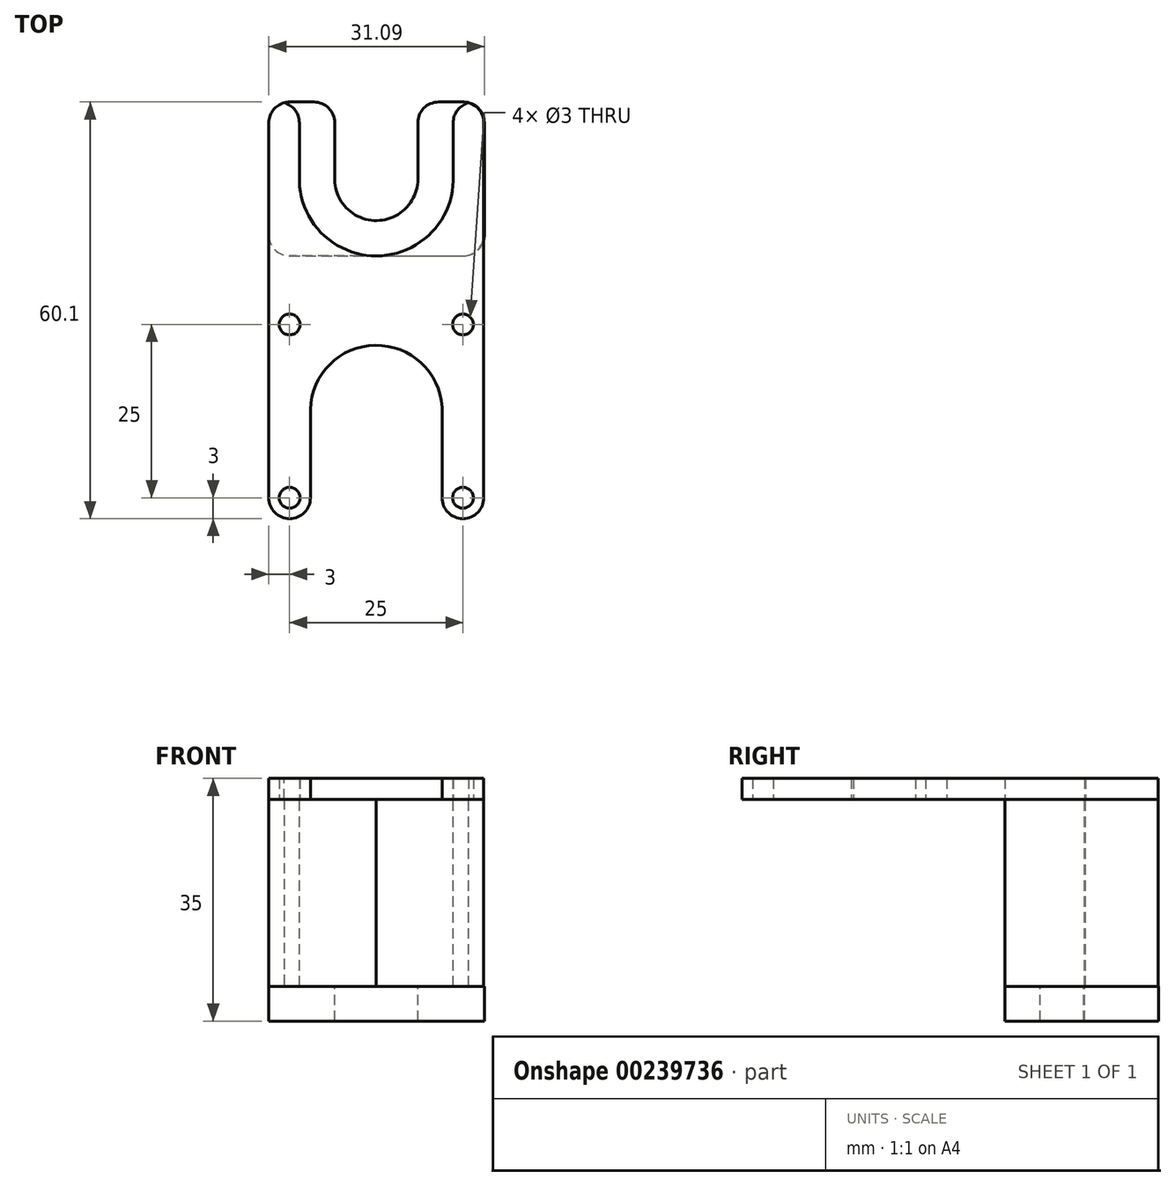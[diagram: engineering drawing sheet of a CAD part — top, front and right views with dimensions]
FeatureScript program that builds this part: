
annotation { "Feature Type Name" : "Feature", "Feature Type Description" : "" }
export const myFeature = defineFeature(function(context is Context, id is Id, definition is map)
    precondition{}
    {
        {
            var Q0;
            Q0=qCreatedBy(makeId("Top.planeOp"),FACE);
            var sketch = newSketch(context, id + "F0", { "sketchPlane" : qUnion([Q0])});
            skCircle(sketch, "E0", {"center": v(-12.5, 0) * mm, "radius": 1.5 * mm});
            skCircle(sketch, "E1", {"center": v(12.5, 0) * mm, "radius": 1.5 * mm});
            skCircle(sketch, "E2", {"center": v(-12.5, 25) * mm, "radius": 1.5 * mm});
            skCircle(sketch, "E3", {"center": v(12.5, 25) * mm, "radius": 1.5 * mm});
            skLineSegment(sketch, "E4.bottom", {"start": v(-15.5, 57.1) * mm, "end": v(-11.1, 57.1) * mm});
            skLineSegment(sketch, "E4.top", {"start": v(-12.5, -3) * mm, "end": v(-12.5, -3) * mm});
            skLineSegment(sketch, "E4.left", {"start": v(-15.5, 57.1) * mm, "end": v(-15.5, 0) * mm});
            skLineSegment(sketch, "E4.right", {"start": v(15.5, 57.1) * mm, "end": v(15.5, 0) * mm});
            skArc(sketch, "E5", {"start": v(9.48, 11.96) * mm, "mid": v(0.16, 22) * mm, "end": v(-9.5, 12.28) * mm});
            skLineSegment(sketch, "E6", {"start": v(-9.5, 12.72) * mm, "end": v(-9.5, 0) * mm});
            skLineSegment(sketch, "E7", {"start": v(9.48, 13.04) * mm, "end": v(9.48, 0) * mm});
            skLineSegment(sketch, "E8.trimOffspring", {"start": v(12.48, -3) * mm, "end": v(12.5, -3) * mm});
            skArc(sketch, "E9", {"start": v(-11.1, 46.4) * mm, "mid": v(0.05, 34.9) * mm, "end": v(11.09, 46.5) * mm});
            skPoint(sketch, "E10.visualSharp", {"position": v(15.5, -3) * mm});
            skArc(sketch, "E10.filletArc", {"start": v(12.5, -3) * mm, "mid": v(14.62, -2.12) * mm, "end": v(15.5, 0) * mm});
            skPoint(sketch, "E11.visualSharp", {"position": v(-15.5, -3) * mm});
            skArc(sketch, "E11.filletArc", {"start": v(-15.5, 0) * mm, "mid": v(-14.62, -2.12) * mm, "end": v(-12.5, -3) * mm});
            skPoint(sketch, "E12.visualSharp", {"position": v(-9.5, -3) * mm});
            skArc(sketch, "E12.filletArc", {"start": v(-12.5, -3) * mm, "mid": v(-10.38, -2.12) * mm, "end": v(-9.5, 0) * mm});
            skPoint(sketch, "E13.visualSharp", {"position": v(9.48, -3) * mm});
            skArc(sketch, "E13.filletArc", {"start": v(9.48, 0) * mm, "mid": v(10.36, -2.12) * mm, "end": v(12.48, -3) * mm});
            skLineSegment(sketch, "E14", {"start": v(-11.1, 46.4) * mm, "end": v(-11.1, 57.1) * mm});
            skLineSegment(sketch, "E15", {"start": v(11.09, 46.5) * mm, "end": v(11.09, 57.1) * mm});
            skLineSegment(sketch, "E16.trimOffspring", {"start": v(11.09, 57.1) * mm, "end": v(15.5, 57.1) * mm});
            skSolve(sketch);
        }
        {
            var Q0;
            Q0 = qSketchRegion(id + "F0", true);
            extrude(context, id + "F1", {"entities" : qUnion([Q0]), "depth" : 3 * mm});
        }
        {
            var Q0;
            Q0=makeQuery(id+"F1.opExtrude","CAP_FACE",FACE,{"disambiguationData":[OSD([sQuery(id+"F0.wireOp",EDGE,"E0"),sQuery(id+"F0.wireOp",EDGE,"E1"),sQuery(id+"F0.wireOp",EDGE,"E2"),sQuery(id+"F0.wireOp",EDGE,"E3"),sQuery(id+"F0.wireOp",EDGE,"E4.bottom"),sQuery(id+"F0.wireOp",EDGE,"E4.top"),sQuery(id+"F0.wireOp",EDGE,"E4.left"),sQuery(id+"F0.wireOp",EDGE,"E4.right"),sQuery(id+"F0.wireOp",EDGE,"E5"),sQuery(id+"F0.wireOp",EDGE,"E6"),sQuery(id+"F0.wireOp",EDGE,"E7"),sQuery(id+"F0.wireOp",EDGE,"E8.trimOffspring"),sQuery(id+"F0.wireOp",EDGE,"E9"),sQuery(id+"F0.wireOp",EDGE,"E10.filletArc"),sQuery(id+"F0.wireOp",EDGE,"E11.filletArc"),sQuery(id+"F0.wireOp",EDGE,"E12.filletArc"),sQuery(id+"F0.wireOp",EDGE,"E13.filletArc"),sQuery(id+"F0.wireOp",EDGE,"E14"),sQuery(id+"F0.wireOp",EDGE,"E15"),sQuery(id+"F0.wireOp",EDGE,"E16.trimOffspring")])],"isStart":true});
            var sketch = newSketch(context, id + "F2", { "sketchPlane" : qUnion([Q0])});
            skLineSegment(sketch, "E17", {"start": v(0, -34.9) * mm, "end": v(-12.5, -34.9) * mm});
            skLineSegment(sketch, "E18", {"start": v(-15.5, -37.9) * mm, "end": v(-15.5, -57.1) * mm});
            skLineSegment(sketch, "E19", {"start": v(-15.5, -57.1) * mm, "end": v(-11.1, -57.1) * mm});
            skLineSegment(sketch, "E20", {"start": v(-11.1, -57.1) * mm, "end": v(-11.1, -46.4) * mm});
            skArc(sketch, "E21", {"start": v(11.09, -46.5) * mm, "mid": v(0.05, -34.9) * mm, "end": v(-11.1, -46.4) * mm});
            skLineSegment(sketch, "E22", {"start": v(0, -34.9) * mm, "end": v(12.5, -34.9) * mm});
            skLineSegment(sketch, "E23", {"start": v(15.5, -37.9) * mm, "end": v(15.5, -57.1) * mm});
            skLineSegment(sketch, "E24", {"start": v(15.5, -57.1) * mm, "end": v(11.09, -57.1) * mm});
            skLineSegment(sketch, "E25", {"start": v(11.09, -57.1) * mm, "end": v(11.09, -46.5) * mm});
            skPoint(sketch, "E26.visualSharp", {"position": v(-15.5, -34.9) * mm});
            skArc(sketch, "E26.filletArc", {"start": v(-12.5, -34.9) * mm, "mid": v(-14.62, -35.78) * mm, "end": v(-15.5, -37.9) * mm});
            skPoint(sketch, "E27.visualSharp", {"position": v(15.5, -34.9) * mm});
            skArc(sketch, "E27.filletArc", {"start": v(15.5, -37.9) * mm, "mid": v(14.62, -35.78) * mm, "end": v(12.5, -34.9) * mm});
            skSolve(sketch);
        }
        {
            var Q0;
            {var subQ1=sQuery(id+"F2.wireOp",EDGE,"E17");Q0=makeQuery(id+"F2.imprint","IMPRINT",FACE,{"disambiguationData":[TD([[makeQuery(id+"F2.imprint","IMPRINT",EDGE,{"derivedFrom":subQ1}),1.0]])]});}
            var Q1;
            {var subQ0=sQuery(id+"F2.wireOp",EDGE,"E22");Q1=makeQuery(id+"F2.imprint","IMPRINT",FACE,{"disambiguationData":[TD([[makeQuery(id+"F2.imprint","IMPRINT",EDGE,{"derivedFrom":subQ0}),-1.0]])]});}
            extrude(context, id + "F3", {"entities" : qUnion([Q0, Q1]), "depth" : 27 * mm});
        }
        {
            var Q0;
            Q0=makeQuery(id+"F3.opExtrude","CAP_FACE",FACE,{"disambiguationData":[OSD([sQuery(id+"F2.wireOp",EDGE,"E17"),sQuery(id+"F2.wireOp",EDGE,"E18"),sQuery(id+"F2.wireOp",EDGE,"E19"),sQuery(id+"F2.wireOp",EDGE,"E20"),sQuery(id+"F2.wireOp",EDGE,"E21"),sQuery(id+"F2.wireOp",EDGE,"E26.filletArc")])],"isStart":false});
            var sketch = newSketch(context, id + "F4", { "sketchPlane" : qUnion([Q0])});
            skArc(sketch, "E28", {"start": v(5.99, -46.4) * mm, "mid": v(0.06, -40) * mm, "end": v(-6, -46.28) * mm});
            skLineSegment(sketch, "E29", {"start": v(-6, -46.28) * mm, "end": v(-6, -54.1) * mm});
            skLineSegment(sketch, "E30", {"start": v(-9, -57.1) * mm, "end": v(-15.5, -57.1) * mm});
            skLineSegment(sketch, "E31", {"start": v(-15.5, -57.1) * mm, "end": v(-15.5, -37.9) * mm});
            skLineSegment(sketch, "E32", {"start": v(-12.5, -34.9) * mm, "end": v(0, -34.9) * mm});
            skLineSegment(sketch, "E33", {"start": v(0, -34.9) * mm, "end": v(12.59, -34.9) * mm});
            skLineSegment(sketch, "E34", {"start": v(15.59, -37.9) * mm, "end": v(15.59, -57.1) * mm});
            skLineSegment(sketch, "E35", {"start": v(15.59, -57.1) * mm, "end": v(8.99, -57.1) * mm});
            skLineSegment(sketch, "E36", {"start": v(5.99, -46.4) * mm, "end": v(5.99, -54.1) * mm});
            skPoint(sketch, "E37.visualSharp", {"position": v(-15.5, -34.9) * mm});
            skArc(sketch, "E37.filletArc", {"start": v(-12.5, -34.9) * mm, "mid": v(-14.62, -35.78) * mm, "end": v(-15.5, -37.9) * mm});
            skPoint(sketch, "E38.visualSharp", {"position": v(15.59, -34.9) * mm});
            skArc(sketch, "E38.filletArc", {"start": v(15.59, -37.9) * mm, "mid": v(14.7, -35.78) * mm, "end": v(12.59, -34.9) * mm});
            skPoint(sketch, "E39.visualSharp", {"position": v(-6, -57.1) * mm});
            skArc(sketch, "E39.filletArc", {"start": v(-9, -57.1) * mm, "mid": v(-6.87, -56.22) * mm, "end": v(-6, -54.1) * mm});
            skPoint(sketch, "E40.visualSharp", {"position": v(5.99, -57.1) * mm});
            skArc(sketch, "E40.filletArc", {"start": v(5.99, -54.1) * mm, "mid": v(6.87, -56.22) * mm, "end": v(8.99, -57.1) * mm});
            skSolve(sketch);
        }
        {
            var Q0;
            Q0 = qSketchRegion(id + "F4", true);
            extrude(context, id + "F5", {"entities" : qUnion([Q0]), "depth" : 5 * mm});
        }
        {
            var Q0;
            Q0=makeQuery(id+"F5.opExtrude","SWEPT_EDGE",EDGE,{"disambiguationData":[OSD([sQuery(id+"F4.wireOp",EDGE,"E30"),sQuery(id+"F4.wireOp",EDGE,"E31")])]});
            var Q1;
            Q1=makeQuery(id+"F3.opExtrude","SWEPT_EDGE",EDGE,{"disambiguationData":[OSD([sQuery(id+"F2.wireOp",EDGE,"E18"),sQuery(id+"F2.wireOp",EDGE,"E19")])]});
            var Q2;
            Q2=makeQuery(id+"F1.opExtrude","SWEPT_EDGE",EDGE,{"disambiguationData":[OSD([sQuery(id+"F0.wireOp",EDGE,"E4.bottom"),sQuery(id+"F0.wireOp",EDGE,"E4.left")])]});
            var Q3;
            Q3=makeQuery(id+"F3.opExtrude","SWEPT_EDGE",EDGE,{"disambiguationData":[OSD([sQuery(id+"F2.wireOp",EDGE,"E19"),sQuery(id+"F2.wireOp",EDGE,"E20")])]});
            var Q4;
            Q4=makeQuery(id+"F1.opExtrude","SWEPT_EDGE",EDGE,{"disambiguationData":[OSD([sQuery(id+"F0.wireOp",EDGE,"E4.bottom"),sQuery(id+"F0.wireOp",EDGE,"E14")])]});
            var Q5;
            Q5=makeQuery(id+"F3.opExtrude","SWEPT_EDGE",EDGE,{"disambiguationData":[OSD([sQuery(id+"F2.wireOp",EDGE,"E24"),sQuery(id+"F2.wireOp",EDGE,"E25")])]});
            var Q6;
            Q6=makeQuery(id+"F1.opExtrude","SWEPT_EDGE",EDGE,{"disambiguationData":[OSD([sQuery(id+"F0.wireOp",EDGE,"E15"),sQuery(id+"F0.wireOp",EDGE,"E16.trimOffspring")])]});
            var Q7;
            Q7=makeQuery(id+"F5.opExtrude","SWEPT_EDGE",EDGE,{"disambiguationData":[OSD([sQuery(id+"F4.wireOp",EDGE,"E34"),sQuery(id+"F4.wireOp",EDGE,"E35")])]});
            var Q8;
            Q8=makeQuery(id+"F3.opExtrude","SWEPT_EDGE",EDGE,{"disambiguationData":[OSD([sQuery(id+"F2.wireOp",EDGE,"E23"),sQuery(id+"F2.wireOp",EDGE,"E24")])]});
            var Q9;
            Q9=makeQuery(id+"F1.opExtrude","SWEPT_EDGE",EDGE,{"disambiguationData":[OSD([sQuery(id+"F0.wireOp",EDGE,"E4.right"),sQuery(id+"F0.wireOp",EDGE,"E16.trimOffspring")])]});
            fillet(context, id + "F6", {"entities" : qUnion([Q0, Q1, Q2, Q3, Q4, Q5, Q6, Q7, Q8, Q9]), "radius" : 3 * mm, "tangentPropagation" : true, "allowEdgeOverflow" : false});
        }
    });
